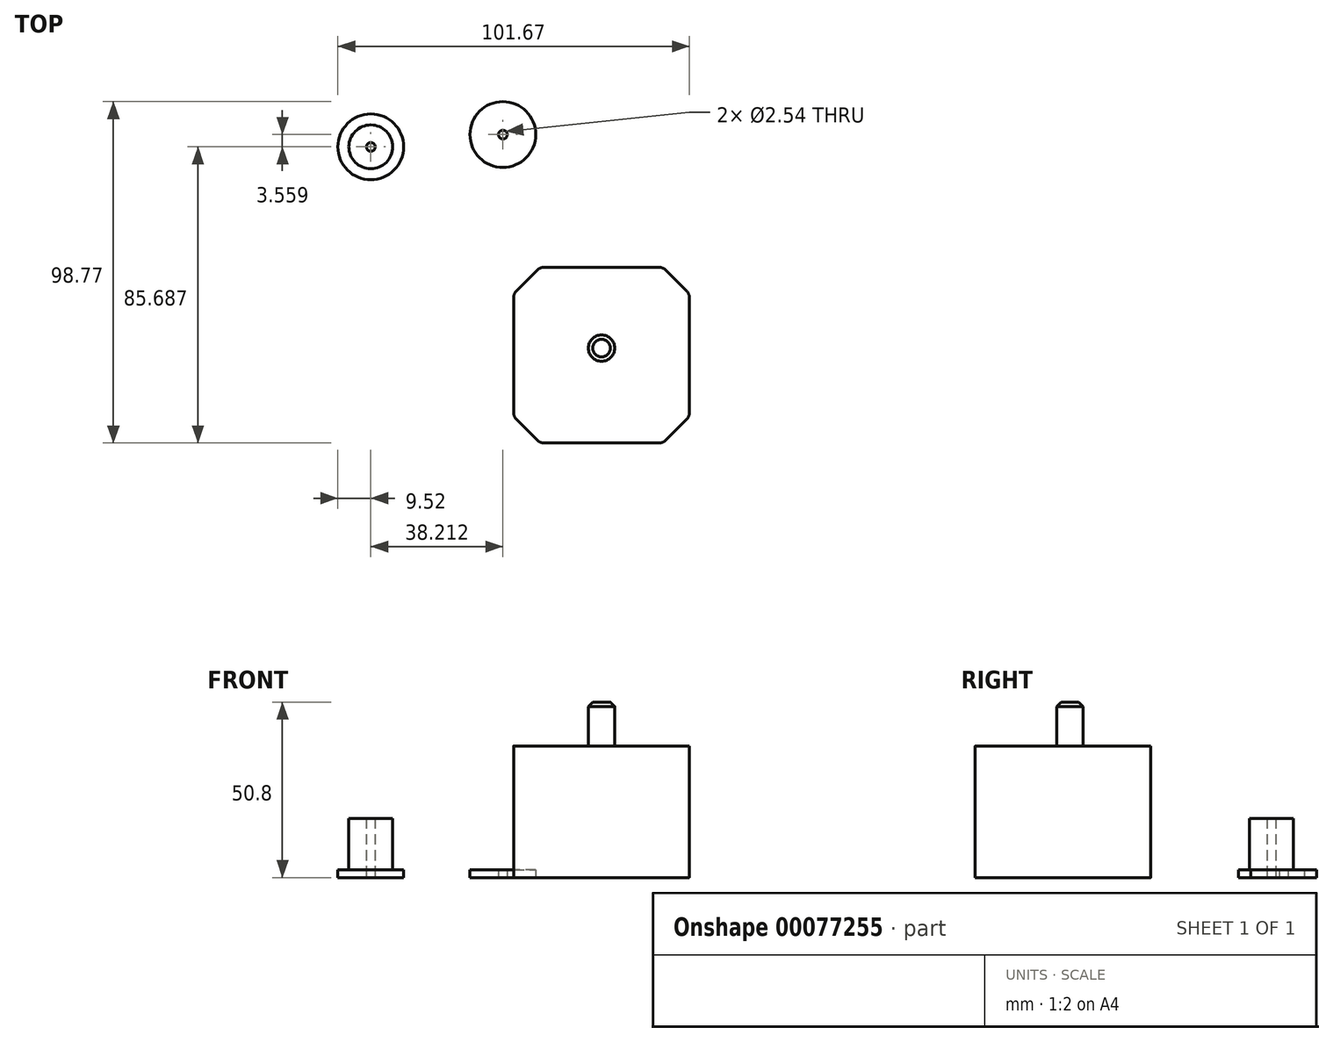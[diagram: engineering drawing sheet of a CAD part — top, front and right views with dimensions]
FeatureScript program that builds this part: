
annotation { "Feature Type Name" : "Feature", "Feature Type Description" : "" }
export const myFeature = defineFeature(function(context is Context, id is Id, definition is map)
    precondition{}
    {
        {
            var Q0;
            Q0=qCreatedBy(makeId("Top.planeOp"),FACE);
            var sketch = newSketch(context, id + "F0", { "sketchPlane" : qUnion([Q0])});
            skLineSegment(sketch, "E0.bottom", {"start": v(25.4, -27.43) * mm, "end": v(-25.4, -27.43) * mm});
            skLineSegment(sketch, "E0.top", {"start": v(25.4, 23.37) * mm, "end": v(-25.4, 23.37) * mm});
            skLineSegment(sketch, "E0.left", {"start": v(25.4, -27.43) * mm, "end": v(25.4, 23.37) * mm});
            skLineSegment(sketch, "E0.right", {"start": v(-25.4, -27.43) * mm, "end": v(-25.4, 23.37) * mm});
            skPoint(sketch, "E0.middle", {"position": v(0, -2.03) * mm});
            skCircle(sketch, "E1", {"center": v(0, 0) * mm, "radius": 3.81 * mm});
            skSolve(sketch);
        }
        {
            var Q0;
            Q0=makeQuery(id+"F0.imprint","IMPRINT",FACE,{"disambiguationData":[TD([[makeQuery(id+"F0.imprint","IMPRINT",EDGE,{"derivedFrom":sQuery(id+"F0.wireOp",EDGE,"E0.bottom")}),-1.0]])]});
            extrude(context, id + "F1", {"entities" : qUnion([Q0]), "depth" : 38.1 * mm});
        }
        {
            var Q0;
            Q0=makeQuery(id+"F0.imprint","IMPRINT",FACE,{"disambiguationData":[TD([[makeQuery(id+"F0.imprint","IMPRINT",EDGE,{"derivedFrom":sQuery(id+"F0.wireOp",EDGE,"E1")}),1.0]])]});
            extrude(context, id + "F2", {"entities" : qUnion([Q0]), "operationType" : NewBodyOperationType.ADD, "depth" : 50.8 * mm});
        }
        {
            var Q0;
            Q0=makeQuery(id+"F1.opExtrude","SWEPT_EDGE",EDGE,{"disambiguationData":[OSD([sQuery(id+"F0.wireOp",EDGE,"E0.bottom"),sQuery(id+"F0.wireOp",EDGE,"E0.right")])]});
            var Q1;
            Q1=makeQuery(id+"F1.opExtrude","SWEPT_EDGE",EDGE,{"disambiguationData":[OSD([sQuery(id+"F0.wireOp",EDGE,"E0.bottom"),sQuery(id+"F0.wireOp",EDGE,"E0.left")])]});
            var Q2;
            Q2=makeQuery(id+"F1.opExtrude","SWEPT_EDGE",EDGE,{"disambiguationData":[OSD([sQuery(id+"F0.wireOp",EDGE,"E0.top"),sQuery(id+"F0.wireOp",EDGE,"E0.left")])]});
            var Q3;
            Q3=makeQuery(id+"F1.opExtrude","SWEPT_EDGE",EDGE,{"disambiguationData":[OSD([sQuery(id+"F0.wireOp",EDGE,"E0.top"),sQuery(id+"F0.wireOp",EDGE,"E0.right")])]});
            chamfer(context, id + "F3", {"entities" : qUnion([Q0, Q1, Q2, Q3]), "width" : 7.62 * mm, "tangentPropagation" : true});
        }
        {
            var Q0;
            {var subQ0=sQuery(id+"F0.wireOp",EDGE,"E0.right");Q0=makeQuery(id+"F3.opChamfer","BLEND_EDGE",EDGE,{"blendedFrom":[makeQuery(id+"F1.opExtrude","SWEPT_EDGE",EDGE,{"disambiguationData":[OSD([sQuery(id+"F0.wireOp",EDGE,"E0.bottom"),subQ0])]}),makeQuery(id+"F1.opExtrude","SWEPT_FACE",FACE,{"disambiguationData":[OSD([subQ0])]})],"blendedInto":[makeQuery(id+"F1.opExtrude","SWEPT_FACE",FACE,{"disambiguationData":[OSD([subQ0])]})]});}
            var Q1;
            {var subQ0=sQuery(id+"F0.wireOp",EDGE,"E0.bottom");Q1=makeQuery(id+"F3.opChamfer","BLEND_EDGE",EDGE,{"blendedFrom":[makeQuery(id+"F1.opExtrude","SWEPT_EDGE",EDGE,{"disambiguationData":[OSD([subQ0,sQuery(id+"F0.wireOp",EDGE,"E0.right")])]}),makeQuery(id+"F1.opExtrude","SWEPT_FACE",FACE,{"disambiguationData":[OSD([subQ0])]})],"blendedInto":[makeQuery(id+"F1.opExtrude","SWEPT_FACE",FACE,{"disambiguationData":[OSD([subQ0])]})]});}
            var Q2;
            {var subQ0=sQuery(id+"F0.wireOp",EDGE,"E0.bottom");Q2=makeQuery(id+"F3.opChamfer","BLEND_EDGE",EDGE,{"blendedFrom":[makeQuery(id+"F1.opExtrude","SWEPT_EDGE",EDGE,{"disambiguationData":[OSD([subQ0,sQuery(id+"F0.wireOp",EDGE,"E0.left")])]}),makeQuery(id+"F1.opExtrude","SWEPT_FACE",FACE,{"disambiguationData":[OSD([subQ0])]})],"blendedInto":[makeQuery(id+"F1.opExtrude","SWEPT_FACE",FACE,{"disambiguationData":[OSD([subQ0])]})]});}
            var Q3;
            {var subQ0=sQuery(id+"F0.wireOp",EDGE,"E0.left");Q3=makeQuery(id+"F3.opChamfer","BLEND_EDGE",EDGE,{"blendedFrom":[makeQuery(id+"F1.opExtrude","SWEPT_EDGE",EDGE,{"disambiguationData":[OSD([sQuery(id+"F0.wireOp",EDGE,"E0.bottom"),subQ0])]}),makeQuery(id+"F1.opExtrude","SWEPT_FACE",FACE,{"disambiguationData":[OSD([subQ0])]})],"blendedInto":[makeQuery(id+"F1.opExtrude","SWEPT_FACE",FACE,{"disambiguationData":[OSD([subQ0])]})]});}
            var Q4;
            {var subQ0=sQuery(id+"F0.wireOp",EDGE,"E0.top");Q4=makeQuery(id+"F3.opChamfer","BLEND_EDGE",EDGE,{"blendedFrom":[makeQuery(id+"F1.opExtrude","SWEPT_EDGE",EDGE,{"disambiguationData":[OSD([subQ0,sQuery(id+"F0.wireOp",EDGE,"E0.left")])]}),makeQuery(id+"F1.opExtrude","SWEPT_FACE",FACE,{"disambiguationData":[OSD([subQ0])]})],"blendedInto":[makeQuery(id+"F1.opExtrude","SWEPT_FACE",FACE,{"disambiguationData":[OSD([subQ0])]})]});}
            var Q5;
            {var subQ0=sQuery(id+"F0.wireOp",EDGE,"E0.left");Q5=makeQuery(id+"F3.opChamfer","BLEND_EDGE",EDGE,{"blendedFrom":[makeQuery(id+"F1.opExtrude","SWEPT_EDGE",EDGE,{"disambiguationData":[OSD([sQuery(id+"F0.wireOp",EDGE,"E0.top"),subQ0])]}),makeQuery(id+"F1.opExtrude","SWEPT_FACE",FACE,{"disambiguationData":[OSD([subQ0])]})],"blendedInto":[makeQuery(id+"F1.opExtrude","SWEPT_FACE",FACE,{"disambiguationData":[OSD([subQ0])]})]});}
            var Q6;
            {var subQ0=sQuery(id+"F0.wireOp",EDGE,"E0.top");Q6=makeQuery(id+"F3.opChamfer","BLEND_EDGE",EDGE,{"blendedFrom":[makeQuery(id+"F1.opExtrude","SWEPT_EDGE",EDGE,{"disambiguationData":[OSD([subQ0,sQuery(id+"F0.wireOp",EDGE,"E0.right")])]}),makeQuery(id+"F1.opExtrude","SWEPT_FACE",FACE,{"disambiguationData":[OSD([subQ0])]})],"blendedInto":[makeQuery(id+"F1.opExtrude","SWEPT_FACE",FACE,{"disambiguationData":[OSD([subQ0])]})]});}
            var Q7;
            {var subQ0=sQuery(id+"F0.wireOp",EDGE,"E0.right");Q7=makeQuery(id+"F3.opChamfer","BLEND_EDGE",EDGE,{"blendedFrom":[makeQuery(id+"F1.opExtrude","SWEPT_EDGE",EDGE,{"disambiguationData":[OSD([sQuery(id+"F0.wireOp",EDGE,"E0.top"),subQ0])]}),makeQuery(id+"F1.opExtrude","SWEPT_FACE",FACE,{"disambiguationData":[OSD([subQ0])]})],"blendedInto":[makeQuery(id+"F1.opExtrude","SWEPT_FACE",FACE,{"disambiguationData":[OSD([subQ0])]})]});}
            fillet(context, id + "F4", {"entities" : qUnion([Q0, Q1, Q2, Q3, Q4, Q5, Q6, Q7]), "radius" : 2.54 * mm, "tangentPropagation" : true, "allowEdgeOverflow" : false});
        }
        {
            var Q0;
            Q0=makeQuery(id+"F2.opExtrude","CAP_EDGE",EDGE,{"disambiguationData":[OSD([sQuery(id+"F0.wireOp",EDGE,"E1")])],"isStart":false});
            chamfer(context, id + "F5", {"entities" : qUnion([Q0]), "width" : 1.27 * mm, "tangentPropagation" : true});
        }
        {
            var Q0;
            Q0=qCreatedBy(makeId("Top.planeOp"),FACE);
            var sketch = newSketch(context, id + "F6", { "sketchPlane" : qUnion([Q0])});
            skCircle(sketch, "E2", {"center": v(-66.75, 58.26) * mm, "radius": 6.35 * mm});
            skCircle(sketch, "E3", {"center": v(-66.75, 58.26) * mm, "radius": 9.52 * mm});
            skCircle(sketch, "E4", {"center": v(-66.75, 58.26) * mm, "radius": 1.27 * mm});
            skCircle(sketch, "E5", {"center": v(-28.54, 61.82) * mm, "radius": 9.53 * mm});
            skCircle(sketch, "E6", {"center": v(-28.54, 61.82) * mm, "radius": 1.27 * mm});
            skSolve(sketch);
        }
        {
            var Q0;
            Q0=makeQuery(id+"F6.imprint","IMPRINT",FACE,{"disambiguationData":[TD([[makeQuery(id+"F6.imprint","IMPRINT",EDGE,{"derivedFrom":sQuery(id+"F6.wireOp",EDGE,"E2")}),-1.0]])]});
            extrude(context, id + "F7", {"entities" : qUnion([Q0]), "depth" : 2.22 * mm});
        }
        {
            var Q0;
            Q0=makeQuery(id+"F6.imprint","IMPRINT",FACE,{"disambiguationData":[TD([[makeQuery(id+"F6.imprint","IMPRINT",EDGE,{"derivedFrom":sQuery(id+"F6.wireOp",EDGE,"E2")}),1.0]])]});
            extrude(context, id + "F8", {"entities" : qUnion([Q0]), "operationType" : NewBodyOperationType.ADD, "depth" : 17.14 * mm});
        }
        {
            var Q0;
            Q0=makeQuery(id+"F6.imprint","IMPRINT",FACE,{"disambiguationData":[TD([[makeQuery(id+"F6.imprint","IMPRINT",EDGE,{"derivedFrom":sQuery(id+"F6.wireOp",EDGE,"E5")}),1.0]])]});
            extrude(context, id + "F9", {"entities" : qUnion([Q0]), "depth" : 2.22 * mm});
        }
    });
